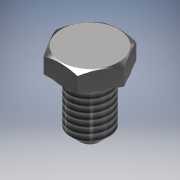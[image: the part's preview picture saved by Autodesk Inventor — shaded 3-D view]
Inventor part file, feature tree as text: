
AUTODESK INVENTOR PART (.ipt)
format: ipt  version: 2018 (Build 220112000, 112)  size: 158,208 bytes
history: native  units: in
note: dims shown in document units (in); Inventor stores cm internally (conversion verified against a paired STEP export)
features: sketch x3, revolve x2, extrude x2, chamfer x1, thread x1, projected_geometry x1
ambient origin geometry x8: Origin, YZ Plane, XZ Plane, XY Plane, X Axis, Y Axis, Z Axis, Center Point
bodies: Solid1 (feature_tree)
feature tree (10):
  revolve  "Revolution1"  [1 undecoded]
  chamfer  "Chamfer1"  Distance=0.125in Angle=45.0deg
  extrude  "Extrusion1"  Depth=0.25in TaperAngle=0.0deg
  extrude  "Extrusion2"  Depth=0.235in TaperAngle=0.0deg
  revolve  "Revolution2"  Angle=30.0deg
  thread  "Thread3"  [1 undecoded]
  sketch  "Sketch1"  dims[d0=0.5in d1=0.75in]
  sketch  "Sketch2"  dims[d2=90.0deg d3=0.125in d4=0.125in d5=45.0deg]
  sketch  "Sketch3"  dims[d6=0.75in d7=0.25in d8=0.0in d9=0.235in d10=0.0in d11=30.0deg d12=90.0deg d17=0.04in d21=1.0in d22=0.0in]
  projected_geometry  "Projected Loop1"
note: 2 required parameter values undecoded (feature->parameter linkage not recoverable at this tier; creation-order binding heuristic only, values carry confidence <= 0.55)